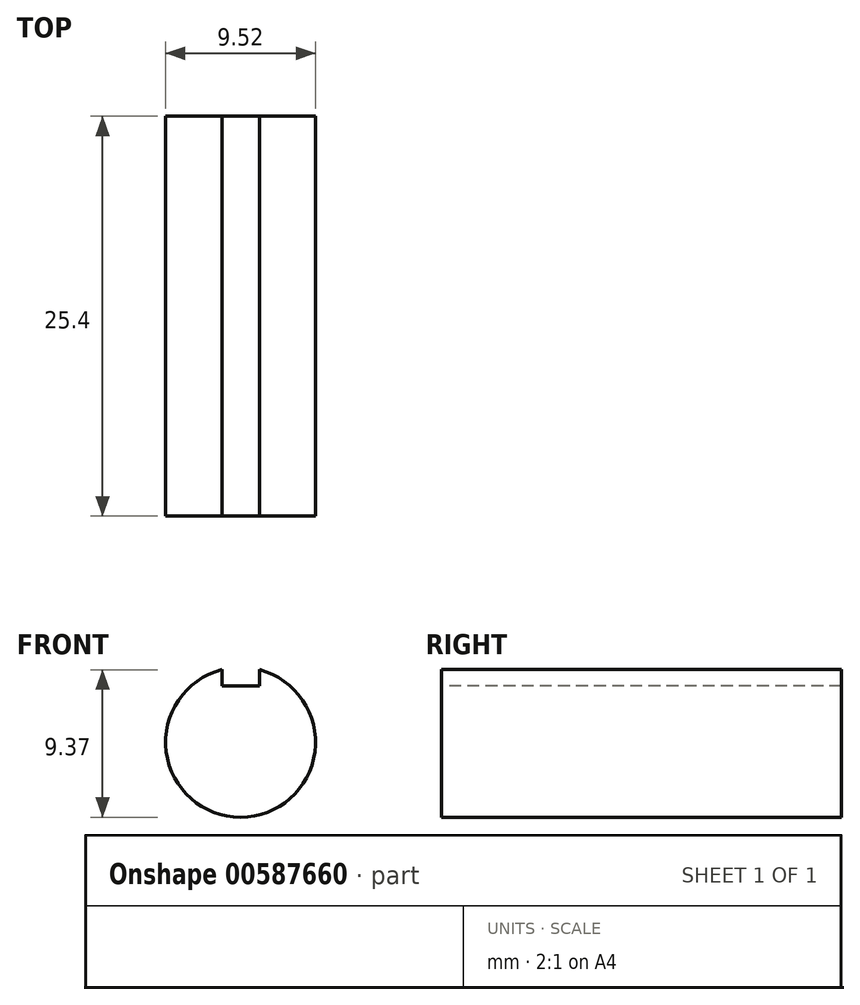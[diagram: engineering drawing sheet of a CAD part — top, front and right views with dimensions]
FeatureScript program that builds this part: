
annotation { "Feature Type Name" : "Feature", "Feature Type Description" : "" }
export const myFeature = defineFeature(function(context is Context, id is Id, definition is map)
    precondition{}
    {
        {
            var Q0;
            Q0=qCreatedBy(makeId("Front.planeOp"),FACE);
            var sketch = newSketch(context, id + "F0", { "sketchPlane" : qUnion([Q0])});
            skCircle(sketch, "E0", {"center": v(0, 0) * mm, "radius": 4.76 * mm});
            skLineSegment(sketch, "E1", {"start": v(0, 0) * mm, "end": v(0, 4.76) * mm, "construction": true});
            skLineSegment(sketch, "E2", {"start": v(-1.2, 4.61) * mm, "end": v(-1.2, 3.57) * mm});
            skLineSegment(sketch, "E3", {"start": v(1.2, 3.57) * mm, "end": v(1.2, 4.61) * mm});
            skLineSegment(sketch, "E4", {"start": v(-1.2, 3.57) * mm, "end": v(0, 3.57) * mm});
            skLineSegment(sketch, "E5", {"start": v(0, 3.57) * mm, "end": v(1.2, 3.57) * mm});
            skSolve(sketch);
        }
        {
            var Q0;
            {var subQ1=sQuery(id+"F0.wireOp",EDGE,"E2");Q0=makeQuery(id+"F0.imprint","IMPRINT",FACE,{"disambiguationData":[TD([[makeQuery(id+"F0.imprint","IMPRINT",EDGE,{"derivedFrom":subQ1}),-1.0]])]});}
            extrude(context, id + "F1", {"entities" : qUnion([Q0]), "oppositeDirection" : true, "depth" : 25.4 * mm, "offsetDistance" : 25.4 * mm});
        }
    });
